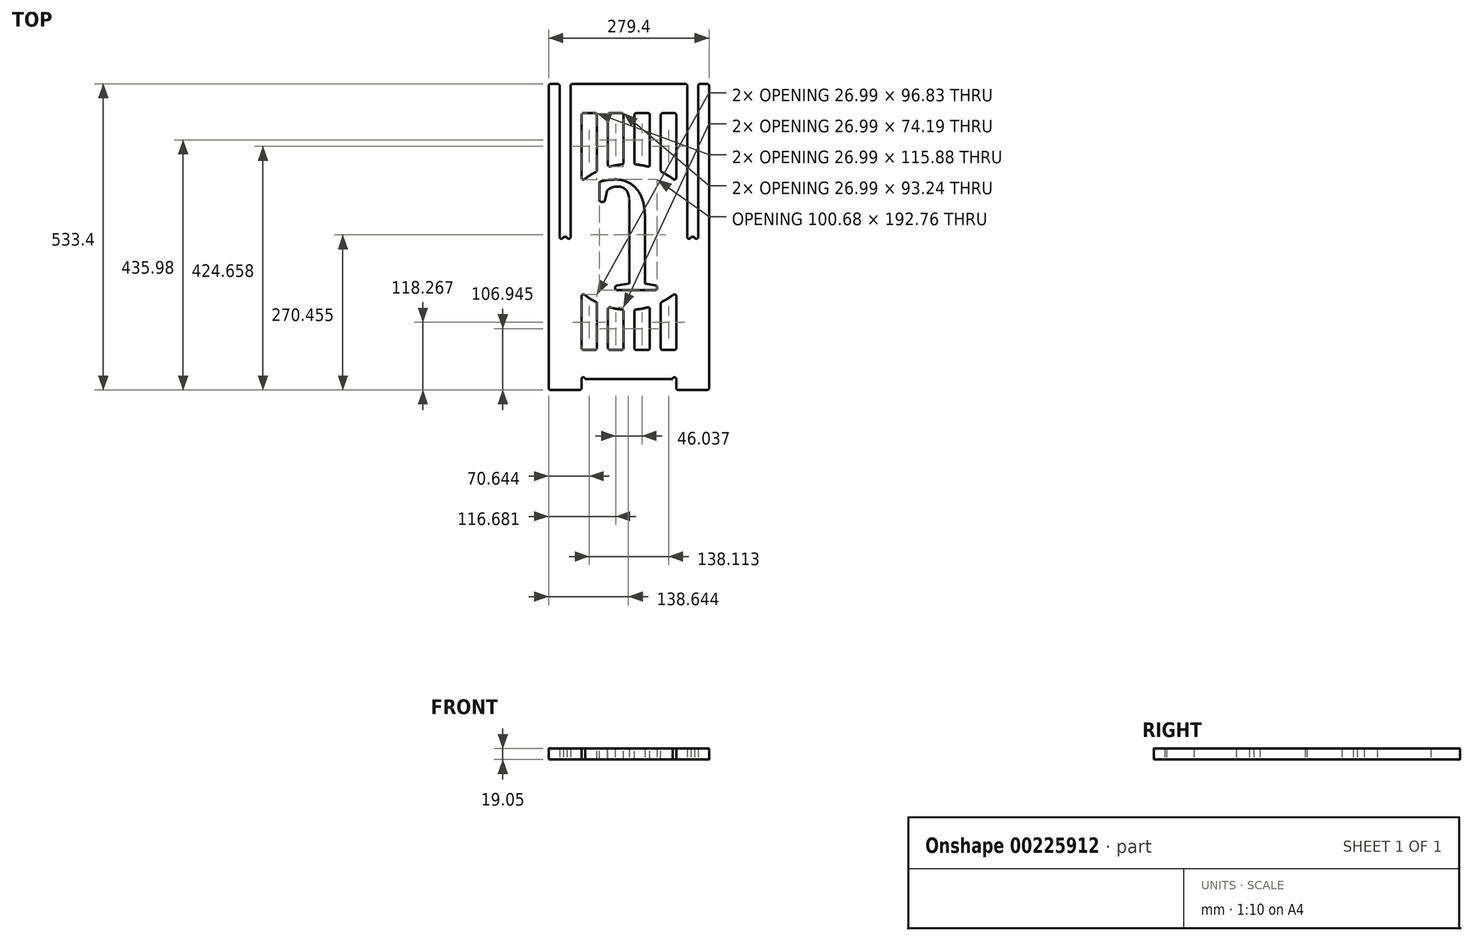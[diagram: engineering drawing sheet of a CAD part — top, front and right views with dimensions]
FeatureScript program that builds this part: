
annotation { "Feature Type Name" : "Feature", "Feature Type Description" : "" }
export const myFeature = defineFeature(function(context is Context, id is Id, definition is map)
    precondition{}
    {
        {
            var Q0;
            Q0=qCreatedBy(makeId("Top.planeOp"),FACE);
            cPlane(context, id + "F0", {"entities" : qUnion([Q0]), "cplaneType" : CPlaneType.OFFSET, "offset" : 19.05 * mm, "width" : 152.4 * mm, "height" : 152.4 * mm});
        }
        {
            var Q0;
            Q0=qCreatedBy(id+"F0.planeOp",FACE);
            var sketch = newSketch(context, id + "F1", { "sketchPlane" : qUnion([Q0])});
            skLineSegment(sketch, "E0", {"start": v(0, -19.05) * mm, "end": v(0, 514.35) * mm});
            skLineSegment(sketch, "E1", {"start": v(0, -19.05) * mm, "end": v(57.15, -19.05) * mm});
            skLineSegment(sketch, "E2", {"start": v(57.15, 0) * mm, "end": v(57.15, -19.05) * mm});
            skLineSegment(sketch, "E3", {"start": v(57.15, 0) * mm, "end": v(222.25, 0) * mm});
            skLineSegment(sketch, "E4", {"start": v(222.25, -19.05) * mm, "end": v(222.25, 0) * mm});
            skLineSegment(sketch, "E5", {"start": v(222.25, -19.05) * mm, "end": v(279.4, -19.05) * mm});
            skLineSegment(sketch, "E6", {"start": v(279.4, 514.35) * mm, "end": v(279.4, -19.05) * mm});
            skLineSegment(sketch, "E7", {"start": v(279.4, 514.35) * mm, "end": v(260.35, 514.35) * mm});
            skLineSegment(sketch, "E8", {"start": v(260.35, 247.65) * mm, "end": v(260.35, 514.35) * mm});
            skLineSegment(sketch, "E9", {"start": v(260.35, 247.65) * mm, "end": v(241.3, 247.65) * mm});
            skLineSegment(sketch, "E10", {"start": v(241.3, 514.35) * mm, "end": v(241.3, 247.65) * mm});
            skLineSegment(sketch, "E11", {"start": v(241.3, 514.35) * mm, "end": v(38.1, 514.35) * mm});
            skLineSegment(sketch, "E12", {"start": v(38.1, 247.65) * mm, "end": v(38.1, 514.35) * mm});
            skLineSegment(sketch, "E13", {"start": v(38.1, 247.65) * mm, "end": v(19.05, 247.65) * mm});
            skLineSegment(sketch, "E14", {"start": v(19.05, 514.35) * mm, "end": v(19.05, 247.65) * mm});
            skLineSegment(sketch, "E15", {"start": v(19.05, 514.35) * mm, "end": v(0, 514.35) * mm});
            skSolve(sketch);
        }
        {
            var Q0;
            Q0 = qSketchRegion(id + "F1", true);
            extrude(context, id + "F2", {"entities" : qUnion([Q0]), "depth" : 19.05 * mm});
        }
        {
            var Q0;
            Q0=makeQuery(id+"F2.opExtrude","SWEPT_EDGE",EDGE,{"disambiguationData":[OSD([sQuery(id+"F1.wireOp",EDGE,"E0"),sQuery(id+"F1.wireOp",EDGE,"E1")])]});
            var Q1;
            Q1=makeQuery(id+"F2.opExtrude","SWEPT_EDGE",EDGE,{"disambiguationData":[OSD([sQuery(id+"F1.wireOp",EDGE,"E1"),sQuery(id+"F1.wireOp",EDGE,"E2")])]});
            var Q2;
            Q2=makeQuery(id+"F2.opExtrude","SWEPT_EDGE",EDGE,{"disambiguationData":[OSD([sQuery(id+"F1.wireOp",EDGE,"E4"),sQuery(id+"F1.wireOp",EDGE,"E5")])]});
            var Q3;
            Q3=makeQuery(id+"F2.opExtrude","SWEPT_EDGE",EDGE,{"disambiguationData":[OSD([sQuery(id+"F1.wireOp",EDGE,"E5"),sQuery(id+"F1.wireOp",EDGE,"E6")])]});
            var Q4;
            Q4=makeQuery(id+"F2.opExtrude","SWEPT_EDGE",EDGE,{"disambiguationData":[OSD([sQuery(id+"F1.wireOp",EDGE,"E0"),sQuery(id+"F1.wireOp",EDGE,"E15")])]});
            var Q5;
            Q5=makeQuery(id+"F2.opExtrude","SWEPT_EDGE",EDGE,{"disambiguationData":[OSD([sQuery(id+"F1.wireOp",EDGE,"E14"),sQuery(id+"F1.wireOp",EDGE,"E15")])]});
            var Q6;
            Q6=makeQuery(id+"F2.opExtrude","SWEPT_EDGE",EDGE,{"disambiguationData":[OSD([sQuery(id+"F1.wireOp",EDGE,"E11"),sQuery(id+"F1.wireOp",EDGE,"E12")])]});
            var Q7;
            Q7=makeQuery(id+"F2.opExtrude","SWEPT_EDGE",EDGE,{"disambiguationData":[OSD([sQuery(id+"F1.wireOp",EDGE,"E10"),sQuery(id+"F1.wireOp",EDGE,"E11")])]});
            var Q8;
            Q8=makeQuery(id+"F2.opExtrude","SWEPT_EDGE",EDGE,{"disambiguationData":[OSD([sQuery(id+"F1.wireOp",EDGE,"E7"),sQuery(id+"F1.wireOp",EDGE,"E8")])]});
            var Q9;
            Q9=makeQuery(id+"F2.opExtrude","SWEPT_EDGE",EDGE,{"disambiguationData":[OSD([sQuery(id+"F1.wireOp",EDGE,"E6"),sQuery(id+"F1.wireOp",EDGE,"E7")])]});
            fillet(context, id + "F3", {"entities" : qUnion([Q0, Q1, Q2, Q3, Q4, Q5, Q6, Q7, Q8, Q9]), "radius" : 3.17 * mm, "tangentPropagation" : true, "allowEdgeOverflow" : false});
        }
        {
            var Q0;
            Q0=makeQuery(id+"F2.opExtrude","CAP_FACE",FACE,{"disambiguationData":[OSD([sQuery(id+"F1.wireOp",EDGE,"E0"),sQuery(id+"F1.wireOp",EDGE,"E1"),sQuery(id+"F1.wireOp",EDGE,"E2"),sQuery(id+"F1.wireOp",EDGE,"E3"),sQuery(id+"F1.wireOp",EDGE,"E4"),sQuery(id+"F1.wireOp",EDGE,"E5"),sQuery(id+"F1.wireOp",EDGE,"E6"),sQuery(id+"F1.wireOp",EDGE,"E7"),sQuery(id+"F1.wireOp",EDGE,"E8"),sQuery(id+"F1.wireOp",EDGE,"E9"),sQuery(id+"F1.wireOp",EDGE,"E10"),sQuery(id+"F1.wireOp",EDGE,"E11"),sQuery(id+"F1.wireOp",EDGE,"E12"),sQuery(id+"F1.wireOp",EDGE,"E13"),sQuery(id+"F1.wireOp",EDGE,"E14"),sQuery(id+"F1.wireOp",EDGE,"E15")])],"isStart":true});
            var sketch = newSketch(context, id + "F4", { "sketchPlane" : qUnion([Q0])});
            skArc(sketch, "E16", {"start": v(57.15, 0) * mm, "mid": v(60.32, -3.18) * mm, "end": v(63.5, 0) * mm});
            skArc(sketch, "E17", {"start": v(222.25, 0) * mm, "mid": v(219.08, -3.18) * mm, "end": v(215.9, 0) * mm});
            skArc(sketch, "E18", {"start": v(19.05, -247.65) * mm, "mid": v(22.23, -244.47) * mm, "end": v(25.4, -247.65) * mm});
            skArc(sketch, "E19", {"start": v(38.1, -247.65) * mm, "mid": v(34.93, -244.47) * mm, "end": v(31.75, -247.65) * mm});
            skArc(sketch, "E20", {"start": v(241.3, -247.65) * mm, "mid": v(244.47, -244.47) * mm, "end": v(247.65, -247.65) * mm});
            skArc(sketch, "E21", {"start": v(260.35, -247.65) * mm, "mid": v(257.17, -244.47) * mm, "end": v(254, -247.65) * mm});
            skLineSegment(sketch, "E22", {"start": v(19.05, -247.65) * mm, "end": v(25.4, -247.65) * mm});
            skLineSegment(sketch, "E23", {"start": v(31.75, -247.65) * mm, "end": v(38.1, -247.65) * mm});
            skLineSegment(sketch, "E24", {"start": v(241.3, -247.65) * mm, "end": v(247.65, -247.65) * mm});
            skLineSegment(sketch, "E25", {"start": v(254, -247.65) * mm, "end": v(260.35, -247.65) * mm});
            skLineSegment(sketch, "E26", {"start": v(57.15, 0) * mm, "end": v(63.5, 0) * mm});
            skLineSegment(sketch, "E27", {"start": v(215.9, 0) * mm, "end": v(222.25, 0) * mm});
            skSolve(sketch);
        }
        {
            var Q0;
            Q0 = qSketchRegion(id + "F4", true);
            extrude(context, id + "F5", {"entities" : qUnion([Q0]), "operationType" : NewBodyOperationType.REMOVE, "oppositeDirection" : true, "depth" : 19.05 * mm});
        }
        {
            var Q0;
            Q0=makeQuery(id+"F2.opExtrude","CAP_FACE",FACE,{"disambiguationData":[OSD([sQuery(id+"F1.wireOp",EDGE,"E0"),sQuery(id+"F1.wireOp",EDGE,"E1"),sQuery(id+"F1.wireOp",EDGE,"E2"),sQuery(id+"F1.wireOp",EDGE,"E3"),sQuery(id+"F1.wireOp",EDGE,"E4"),sQuery(id+"F1.wireOp",EDGE,"E5"),sQuery(id+"F1.wireOp",EDGE,"E6"),sQuery(id+"F1.wireOp",EDGE,"E7"),sQuery(id+"F1.wireOp",EDGE,"E8"),sQuery(id+"F1.wireOp",EDGE,"E9"),sQuery(id+"F1.wireOp",EDGE,"E10"),sQuery(id+"F1.wireOp",EDGE,"E11"),sQuery(id+"F1.wireOp",EDGE,"E12"),sQuery(id+"F1.wireOp",EDGE,"E13"),sQuery(id+"F1.wireOp",EDGE,"E14"),sQuery(id+"F1.wireOp",EDGE,"E15")])],"isStart":true});
            var sketch = newSketch(context, id + "F6", { "sketchPlane" : qUnion([Q0])});
            skText(sketch, "E28", { "text": "J", "fontName": "Tinos-Regular.ttf"});
            skLineSegment(sketch, "E29", {"start": v(0, -247.65) * mm, "end": v(279.4, -247.65) * mm, "construction": true});
            skEllipse(sketch, "E30", {"center": v(139.7, -247.65) * mm, "majorRadius": 127 * mm, "minorRadius": 127 * mm, "majorAxis": v(0, 1), "construction": true});
            skLineSegment(sketch, "E31", {"start": v(139.7, -247.65) * mm, "end": v(139.7, -120.65) * mm, "construction": true});
            skPoint(sketch, "E32", {"position": v(12.7, -247.65) * mm});
            skLineSegment(sketch, "E33.bottom", {"start": v(57.15, -50.8) * mm, "end": v(222.25, -50.8) * mm, "construction": true});
            skLineSegment(sketch, "E33.top", {"start": v(57.15, -463.55) * mm, "end": v(222.25, -463.55) * mm, "construction": true});
            skLineSegment(sketch, "E33.left", {"start": v(57.15, -50.8) * mm, "end": v(57.15, -463.55) * mm, "construction": true});
            skLineSegment(sketch, "E33.right", {"start": v(222.25, -50.8) * mm, "end": v(222.25, -463.55) * mm, "construction": true});
            skPoint(sketch, "E34", {"position": v(72, -140.2) * mm});
            skPoint(sketch, "E35", {"position": v(14.67, -269.95) * mm});
            skPoint(sketch, "E36", {"position": v(160.49, -122.36) * mm});
            skPoint(sketch, "E37", {"position": v(212.8, -143.8) * mm});
            skPoint(sketch, "E38", {"position": v(72.6, -355.48) * mm});
            skPoint(sketch, "E39", {"position": v(114.46, -372.12) * mm});
            skPoint(sketch, "E40", {"position": v(14.69, -270.04) * mm});
            skPoint(sketch, "E41", {"position": v(242.8, -321.81) * mm});
            skLineSegment(sketch, "E42", {"start": v(57.15, -151.14) * mm, "end": v(57.15, -50.8) * mm});
            skLineSegment(sketch, "E43", {"start": v(84.14, -50.8) * mm, "end": v(84.14, -133.45) * mm});
            skLineSegment(sketch, "E44", {"start": v(103.19, -126.01) * mm, "end": v(103.19, -50.8) * mm});
            skLineSegment(sketch, "E45", {"start": v(103.19, -50.8) * mm, "end": v(130.18, -50.8) * mm});
            skLineSegment(sketch, "E46", {"start": v(130.18, -50.8) * mm, "end": v(130.18, -121) * mm});
            skLineSegment(sketch, "E47", {"start": v(149.23, -121) * mm, "end": v(149.23, -50.8) * mm});
            skLineSegment(sketch, "E48", {"start": v(149.23, -50.8) * mm, "end": v(176.21, -50.8) * mm});
            skLineSegment(sketch, "E49", {"start": v(176.21, -50.8) * mm, "end": v(176.21, -126.01) * mm});
            skLineSegment(sketch, "E50", {"start": v(195.26, -133.45) * mm, "end": v(195.26, -50.8) * mm});
            skLineSegment(sketch, "E51", {"start": v(195.26, -50.8) * mm, "end": v(222.25, -50.8) * mm});
            skLineSegment(sketch, "E52", {"start": v(57.15, -344.16) * mm, "end": v(57.15, -463.55) * mm});
            skLineSegment(sketch, "E53", {"start": v(84.14, -463.55) * mm, "end": v(84.14, -361.85) * mm});
            skLineSegment(sketch, "E54", {"start": v(103.19, -369.29) * mm, "end": v(103.19, -463.55) * mm});
            skLineSegment(sketch, "E55", {"start": v(103.19, -463.55) * mm, "end": v(130.18, -463.55) * mm});
            skLineSegment(sketch, "E56", {"start": v(130.18, -463.55) * mm, "end": v(130.18, -374.3) * mm});
            skLineSegment(sketch, "E57", {"start": v(149.23, -463.55) * mm, "end": v(176.21, -463.55) * mm});
            skLineSegment(sketch, "E58", {"start": v(176.21, -463.55) * mm, "end": v(176.21, -369.29) * mm});
            skLineSegment(sketch, "E59", {"start": v(195.26, -361.85) * mm, "end": v(195.26, -463.55) * mm});
            skLineSegment(sketch, "E60", {"start": v(195.26, -463.55) * mm, "end": v(222.25, -463.55) * mm});
            skLineSegment(sketch, "E61", {"start": v(149.23, -463.55) * mm, "end": v(149.23, -374.3) * mm});
            skLineSegment(sketch, "E62", {"start": v(57.15, -418.24) * mm, "end": v(84.14, -418.24) * mm, "construction": true});
            skLineSegment(sketch, "E63", {"start": v(103.19, -421.25) * mm, "end": v(130.18, -421.25) * mm, "construction": true});
            skLineSegment(sketch, "E64", {"start": v(149.23, -416.29) * mm, "end": v(176.21, -416.29) * mm, "construction": true});
            skLineSegment(sketch, "E65", {"start": v(195.26, -412.7) * mm, "end": v(222.25, -412.7) * mm, "construction": true});
            skLineSegment(sketch, "E66", {"start": v(222.25, -344.16) * mm, "end": v(222.25, -463.55) * mm});
            skArc(sketch, "E67", {"start": v(57.15, -344.16) * mm, "mid": v(70.08, -353.87) * mm, "end": v(84.14, -361.85) * mm});
            skArc(sketch, "E68", {"start": v(103.19, -369.29) * mm, "mid": v(116.55, -372.52) * mm, "end": v(130.18, -374.3) * mm});
            skArc(sketch, "E69", {"start": v(149.23, -374.3) * mm, "mid": v(162.85, -372.52) * mm, "end": v(176.21, -369.29) * mm});
            skArc(sketch, "E70", {"start": v(195.26, -361.85) * mm, "mid": v(209.32, -353.87) * mm, "end": v(222.25, -344.16) * mm});
            skLineSegment(sketch, "E71", {"start": v(57.15, -463.55) * mm, "end": v(84.14, -463.55) * mm});
            skLineSegment(sketch, "E72", {"start": v(57.15, -50.8) * mm, "end": v(84.14, -50.8) * mm});
            skLineSegment(sketch, "E73", {"start": v(222.25, -50.8) * mm, "end": v(222.25, -151.14) * mm});
            skLineSegment(sketch, "E74", {"start": v(57.15, -80.06) * mm, "end": v(84.14, -80.06) * mm, "construction": true});
            skLineSegment(sketch, "E75", {"start": v(103.19, -97.63) * mm, "end": v(130.18, -97.63) * mm, "construction": true});
            skLineSegment(sketch, "E76", {"start": v(149.23, -95.67) * mm, "end": v(176.21, -95.67) * mm, "construction": true});
            skLineSegment(sketch, "E77", {"start": v(195.26, -79.24) * mm, "end": v(222.25, -79.24) * mm, "construction": true});
            skArc(sketch, "E78", {"start": v(84.14, -133.45) * mm, "mid": v(70.08, -141.43) * mm, "end": v(57.15, -151.14) * mm});
            skArc(sketch, "E79", {"start": v(130.18, -121) * mm, "mid": v(116.55, -122.78) * mm, "end": v(103.19, -126.01) * mm});
            skArc(sketch, "E80", {"start": v(176.21, -126.01) * mm, "mid": v(162.85, -122.78) * mm, "end": v(149.23, -121) * mm});
            skArc(sketch, "E81", {"start": v(222.25, -151.14) * mm, "mid": v(209.32, -141.43) * mm, "end": v(195.26, -133.45) * mm});
            const initialGuessF6  = {"E28": [0.08223, -0.34493, 1, 0, 0.2088]};
            skSetInitialGuess(sketch, initialGuessF6);
            skSolve(sketch);
        }
        {
            var Q0;
            Q0 = qSketchRegion(id + "F6", true);
            extrude(context, id + "F7", {"entities" : qUnion([Q0]), "operationType" : NewBodyOperationType.REMOVE, "oppositeDirection" : true, "depth" : 25.4 * mm});
        }
        {
            var Q0;
            Q0=makeQuery(id+"F7.boolean.opBoolean","COPY",EDGE,{"derivedFrom":makeQuery(id+"F7.opExtrude","SWEPT_EDGE",EDGE,{"disambiguationData":[OSD([sQuery(id+"F6.wireOp",EDGE,"E42"),sQuery(id+"F6.wireOp",EDGE,"E72")])]})});
            var Q1;
            Q1=makeQuery(id+"F7.boolean.opBoolean","COPY",EDGE,{"derivedFrom":makeQuery(id+"F7.opExtrude","SWEPT_EDGE",EDGE,{"disambiguationData":[OSD([sQuery(id+"F6.wireOp",EDGE,"E44"),sQuery(id+"F6.wireOp",EDGE,"E45")])]})});
            var Q2;
            Q2=makeQuery(id+"F7.boolean.opBoolean","COPY",EDGE,{"derivedFrom":makeQuery(id+"F7.opExtrude","SWEPT_EDGE",EDGE,{"disambiguationData":[OSD([sQuery(id+"F6.wireOp",EDGE,"E47"),sQuery(id+"F6.wireOp",EDGE,"E48")])]})});
            var Q3;
            Q3=makeQuery(id+"F7.boolean.opBoolean","COPY",EDGE,{"derivedFrom":makeQuery(id+"F7.opExtrude","SWEPT_EDGE",EDGE,{"disambiguationData":[OSD([sQuery(id+"F6.wireOp",EDGE,"E50"),sQuery(id+"F6.wireOp",EDGE,"E51")])]})});
            var Q4;
            Q4=makeQuery(id+"F7.boolean.opBoolean","COPY",EDGE,{"derivedFrom":makeQuery(id+"F7.opExtrude","SWEPT_EDGE",EDGE,{"disambiguationData":[OSD([sQuery(id+"F6.wireOp",EDGE,"E43"),sQuery(id+"F6.wireOp",EDGE,"E72")])]})});
            var Q5;
            Q5=makeQuery(id+"F7.boolean.opBoolean","COPY",EDGE,{"derivedFrom":makeQuery(id+"F7.opExtrude","SWEPT_EDGE",EDGE,{"disambiguationData":[OSD([sQuery(id+"F6.wireOp",EDGE,"E45"),sQuery(id+"F6.wireOp",EDGE,"E46")])]})});
            var Q6;
            Q6=makeQuery(id+"F7.boolean.opBoolean","COPY",EDGE,{"derivedFrom":makeQuery(id+"F7.opExtrude","SWEPT_EDGE",EDGE,{"disambiguationData":[OSD([sQuery(id+"F6.wireOp",EDGE,"E48"),sQuery(id+"F6.wireOp",EDGE,"E49")])]})});
            var Q7;
            Q7=makeQuery(id+"F7.boolean.opBoolean","COPY",EDGE,{"derivedFrom":makeQuery(id+"F7.opExtrude","SWEPT_EDGE",EDGE,{"disambiguationData":[OSD([sQuery(id+"F6.wireOp",EDGE,"E51"),sQuery(id+"F6.wireOp",EDGE,"E73")])]})});
            var Q8;
            Q8=makeQuery(id+"F7.boolean.opBoolean","COPY",EDGE,{"derivedFrom":makeQuery(id+"F7.opExtrude","SWEPT_EDGE",EDGE,{"disambiguationData":[OSD([sQuery(id+"F6.wireOp",EDGE,"E42"),sQuery(id+"F6.wireOp",EDGE,"E78")])]})});
            var Q9;
            Q9=makeQuery(id+"F7.boolean.opBoolean","COPY",EDGE,{"derivedFrom":makeQuery(id+"F7.opExtrude","SWEPT_EDGE",EDGE,{"disambiguationData":[OSD([sQuery(id+"F6.wireOp",EDGE,"E44"),sQuery(id+"F6.wireOp",EDGE,"E79")])]})});
            var Q10;
            Q10=makeQuery(id+"F7.boolean.opBoolean","COPY",EDGE,{"derivedFrom":makeQuery(id+"F7.opExtrude","SWEPT_EDGE",EDGE,{"disambiguationData":[OSD([sQuery(id+"F6.wireOp",EDGE,"E47"),sQuery(id+"F6.wireOp",EDGE,"E80")])]})});
            var Q11;
            Q11=makeQuery(id+"F7.boolean.opBoolean","COPY",EDGE,{"derivedFrom":makeQuery(id+"F7.opExtrude","SWEPT_EDGE",EDGE,{"disambiguationData":[OSD([sQuery(id+"F6.wireOp",EDGE,"E50"),sQuery(id+"F6.wireOp",EDGE,"E81")])]})});
            var Q12;
            Q12=makeQuery(id+"F7.boolean.opBoolean","COPY",EDGE,{"derivedFrom":makeQuery(id+"F7.opExtrude","SWEPT_EDGE",EDGE,{"disambiguationData":[OSD([sQuery(id+"F6.wireOp",EDGE,"E43"),sQuery(id+"F6.wireOp",EDGE,"E78")])]})});
            var Q13;
            Q13=makeQuery(id+"F7.boolean.opBoolean","COPY",EDGE,{"derivedFrom":makeQuery(id+"F7.opExtrude","SWEPT_EDGE",EDGE,{"disambiguationData":[OSD([sQuery(id+"F6.wireOp",EDGE,"E46"),sQuery(id+"F6.wireOp",EDGE,"E79")])]})});
            var Q14;
            Q14=makeQuery(id+"F7.boolean.opBoolean","COPY",EDGE,{"derivedFrom":makeQuery(id+"F7.opExtrude","SWEPT_EDGE",EDGE,{"disambiguationData":[OSD([sQuery(id+"F6.wireOp",EDGE,"E49"),sQuery(id+"F6.wireOp",EDGE,"E80")])]})});
            var Q15;
            Q15=makeQuery(id+"F7.boolean.opBoolean","COPY",EDGE,{"derivedFrom":makeQuery(id+"F7.opExtrude","SWEPT_EDGE",EDGE,{"disambiguationData":[OSD([sQuery(id+"F6.wireOp",EDGE,"E73"),sQuery(id+"F6.wireOp",EDGE,"E81")])]})});
            var Q16;
            Q16=makeQuery(id+"F7.boolean.opBoolean","COPY",EDGE,{"derivedFrom":makeQuery(id+"F7.opExtrude","SWEPT_EDGE",EDGE,{"disambiguationData":[OSD([sQuery(id+"F6.wireOp",EDGE,"E53"),sQuery(id+"F6.wireOp",EDGE,"E71")])]})});
            var Q17;
            Q17=makeQuery(id+"F7.boolean.opBoolean","COPY",EDGE,{"derivedFrom":makeQuery(id+"F7.opExtrude","SWEPT_EDGE",EDGE,{"disambiguationData":[OSD([sQuery(id+"F6.wireOp",EDGE,"E55"),sQuery(id+"F6.wireOp",EDGE,"E56")])]})});
            var Q18;
            Q18=makeQuery(id+"F7.boolean.opBoolean","COPY",EDGE,{"derivedFrom":makeQuery(id+"F7.opExtrude","SWEPT_EDGE",EDGE,{"disambiguationData":[OSD([sQuery(id+"F6.wireOp",EDGE,"E57"),sQuery(id+"F6.wireOp",EDGE,"E58")])]})});
            var Q19;
            Q19=makeQuery(id+"F7.boolean.opBoolean","COPY",EDGE,{"derivedFrom":makeQuery(id+"F7.opExtrude","SWEPT_EDGE",EDGE,{"disambiguationData":[OSD([sQuery(id+"F6.wireOp",EDGE,"E60"),sQuery(id+"F6.wireOp",EDGE,"E66")])]})});
            var Q20;
            Q20=makeQuery(id+"F7.boolean.opBoolean","COPY",EDGE,{"derivedFrom":makeQuery(id+"F7.opExtrude","SWEPT_EDGE",EDGE,{"disambiguationData":[OSD([sQuery(id+"F6.wireOp",EDGE,"E59"),sQuery(id+"F6.wireOp",EDGE,"E60")])]})});
            var Q21;
            Q21=makeQuery(id+"F7.boolean.opBoolean","COPY",EDGE,{"derivedFrom":makeQuery(id+"F7.opExtrude","SWEPT_EDGE",EDGE,{"disambiguationData":[OSD([sQuery(id+"F6.wireOp",EDGE,"E57"),sQuery(id+"F6.wireOp",EDGE,"E61")])]})});
            var Q22;
            Q22=makeQuery(id+"F7.boolean.opBoolean","COPY",EDGE,{"derivedFrom":makeQuery(id+"F7.opExtrude","SWEPT_EDGE",EDGE,{"disambiguationData":[OSD([sQuery(id+"F6.wireOp",EDGE,"E54"),sQuery(id+"F6.wireOp",EDGE,"E55")])]})});
            var Q23;
            Q23=makeQuery(id+"F7.boolean.opBoolean","COPY",EDGE,{"derivedFrom":makeQuery(id+"F7.opExtrude","SWEPT_EDGE",EDGE,{"disambiguationData":[OSD([sQuery(id+"F6.wireOp",EDGE,"E52"),sQuery(id+"F6.wireOp",EDGE,"E71")])]})});
            var Q24;
            Q24=makeQuery(id+"F7.boolean.opBoolean","COPY",EDGE,{"derivedFrom":makeQuery(id+"F7.opExtrude","SWEPT_EDGE",EDGE,{"disambiguationData":[OSD([sQuery(id+"F6.wireOp",EDGE,"E53"),sQuery(id+"F6.wireOp",EDGE,"E67")])]})});
            var Q25;
            Q25=makeQuery(id+"F7.boolean.opBoolean","COPY",EDGE,{"derivedFrom":makeQuery(id+"F7.opExtrude","SWEPT_EDGE",EDGE,{"disambiguationData":[OSD([sQuery(id+"F6.wireOp",EDGE,"E56"),sQuery(id+"F6.wireOp",EDGE,"E68")])]})});
            var Q26;
            Q26=makeQuery(id+"F7.boolean.opBoolean","COPY",EDGE,{"derivedFrom":makeQuery(id+"F7.opExtrude","SWEPT_EDGE",EDGE,{"disambiguationData":[OSD([sQuery(id+"F6.wireOp",EDGE,"E58"),sQuery(id+"F6.wireOp",EDGE,"E69")])]})});
            var Q27;
            Q27=makeQuery(id+"F7.boolean.opBoolean","COPY",EDGE,{"derivedFrom":makeQuery(id+"F7.opExtrude","SWEPT_EDGE",EDGE,{"disambiguationData":[OSD([sQuery(id+"F6.wireOp",EDGE,"E66"),sQuery(id+"F6.wireOp",EDGE,"E70")])]})});
            var Q28;
            Q28=makeQuery(id+"F7.boolean.opBoolean","COPY",EDGE,{"derivedFrom":makeQuery(id+"F7.opExtrude","SWEPT_EDGE",EDGE,{"disambiguationData":[OSD([sQuery(id+"F6.wireOp",EDGE,"E59"),sQuery(id+"F6.wireOp",EDGE,"E70")])]})});
            var Q29;
            Q29=makeQuery(id+"F7.boolean.opBoolean","COPY",EDGE,{"derivedFrom":makeQuery(id+"F7.opExtrude","SWEPT_EDGE",EDGE,{"disambiguationData":[OSD([sQuery(id+"F6.wireOp",EDGE,"E61"),sQuery(id+"F6.wireOp",EDGE,"E69")])]})});
            var Q30;
            Q30=makeQuery(id+"F7.boolean.opBoolean","COPY",EDGE,{"derivedFrom":makeQuery(id+"F7.opExtrude","SWEPT_EDGE",EDGE,{"disambiguationData":[OSD([sQuery(id+"F6.wireOp",EDGE,"E54"),sQuery(id+"F6.wireOp",EDGE,"E68")])]})});
            var Q31;
            Q31=makeQuery(id+"F7.boolean.opBoolean","COPY",EDGE,{"derivedFrom":makeQuery(id+"F7.opExtrude","SWEPT_EDGE",EDGE,{"disambiguationData":[OSD([sQuery(id+"F6.wireOp",EDGE,"E52"),sQuery(id+"F6.wireOp",EDGE,"E67")])]})});
            var Q32;
            Q32=makeQuery(id+"F7.boolean.opBoolean","COPY",EDGE,{"derivedFrom":makeQuery(id+"F7.opExtrude","SWEPT_EDGE",EDGE,{"disambiguationData":[OSD([sQuery(id+"F6.wireOp",EDGE,"E28.sketch_text.stroke-10"),sQuery(id+"F6.wireOp",EDGE,"E28.sketch_text.stroke-11")])]})});
            var Q33;
            Q33=makeQuery(id+"F7.boolean.opBoolean","COPY",EDGE,{"derivedFrom":makeQuery(id+"F7.opExtrude","SWEPT_EDGE",EDGE,{"disambiguationData":[OSD([sQuery(id+"F6.wireOp",EDGE,"E28.sketch_text.stroke-11"),sQuery(id+"F6.wireOp",EDGE,"E28.sketch_text.stroke-12")])]})});
            var Q34;
            Q34=makeQuery(id+"F7.boolean.opBoolean","COPY",EDGE,{"derivedFrom":makeQuery(id+"F7.opExtrude","SWEPT_EDGE",EDGE,{"disambiguationData":[OSD([sQuery(id+"F6.wireOp",EDGE,"E28.sketch_text.stroke-9"),sQuery(id+"F6.wireOp",EDGE,"E28.sketch_text.stroke-10")])]})});
            var Q35;
            Q35=makeQuery(id+"F7.boolean.opBoolean","COPY",EDGE,{"derivedFrom":makeQuery(id+"F7.opExtrude","SWEPT_EDGE",EDGE,{"disambiguationData":[OSD([sQuery(id+"F6.wireOp",EDGE,"E28.sketch_text.stroke-2"),sQuery(id+"F6.wireOp",EDGE,"E28.sketch_text.stroke-3")])]})});
            var Q36;
            Q36=makeQuery(id+"F7.boolean.opBoolean","COPY",EDGE,{"derivedFrom":makeQuery(id+"F7.opExtrude","SWEPT_EDGE",EDGE,{"disambiguationData":[OSD([sQuery(id+"F6.wireOp",EDGE,"E28.sketch_text.stroke-3"),sQuery(id+"F6.wireOp",EDGE,"E28.sketch_text.stroke-4")])]})});
            var Q37;
            Q37=makeQuery(id+"F7.boolean.opBoolean","COPY",EDGE,{"derivedFrom":makeQuery(id+"F7.opExtrude","SWEPT_EDGE",EDGE,{"disambiguationData":[OSD([sQuery(id+"F6.wireOp",EDGE,"E28.sketch_text.stroke-1"),sQuery(id+"F6.wireOp",EDGE,"E28.sketch_text.stroke-2")])]})});
            var Q38;
            Q38=makeQuery(id+"F7.boolean.opBoolean","COPY",EDGE,{"derivedFrom":makeQuery(id+"F7.opExtrude","SWEPT_EDGE",EDGE,{"disambiguationData":[OSD([sQuery(id+"F6.wireOp",EDGE,"E28.sketch_text.stroke-0"),sQuery(id+"F6.wireOp",EDGE,"E28.sketch_text.stroke-1")])]})});
            fillet(context, id + "F8", {"entities" : qUnion([Q0, Q1, Q2, Q3, Q4, Q5, Q6, Q7, Q8, Q9, Q10, Q11, Q12, Q13, Q14, Q15, Q16, Q17, Q18, Q19, Q20, Q21, Q22, Q23, Q24, Q25, Q26, Q27, Q28, Q29, Q30, Q31, Q32, Q33, Q34, Q35, Q36, Q37, Q38]), "radius" : 3.17 * mm, "tangentPropagation" : true, "allowEdgeOverflow" : false});
        }
    });
